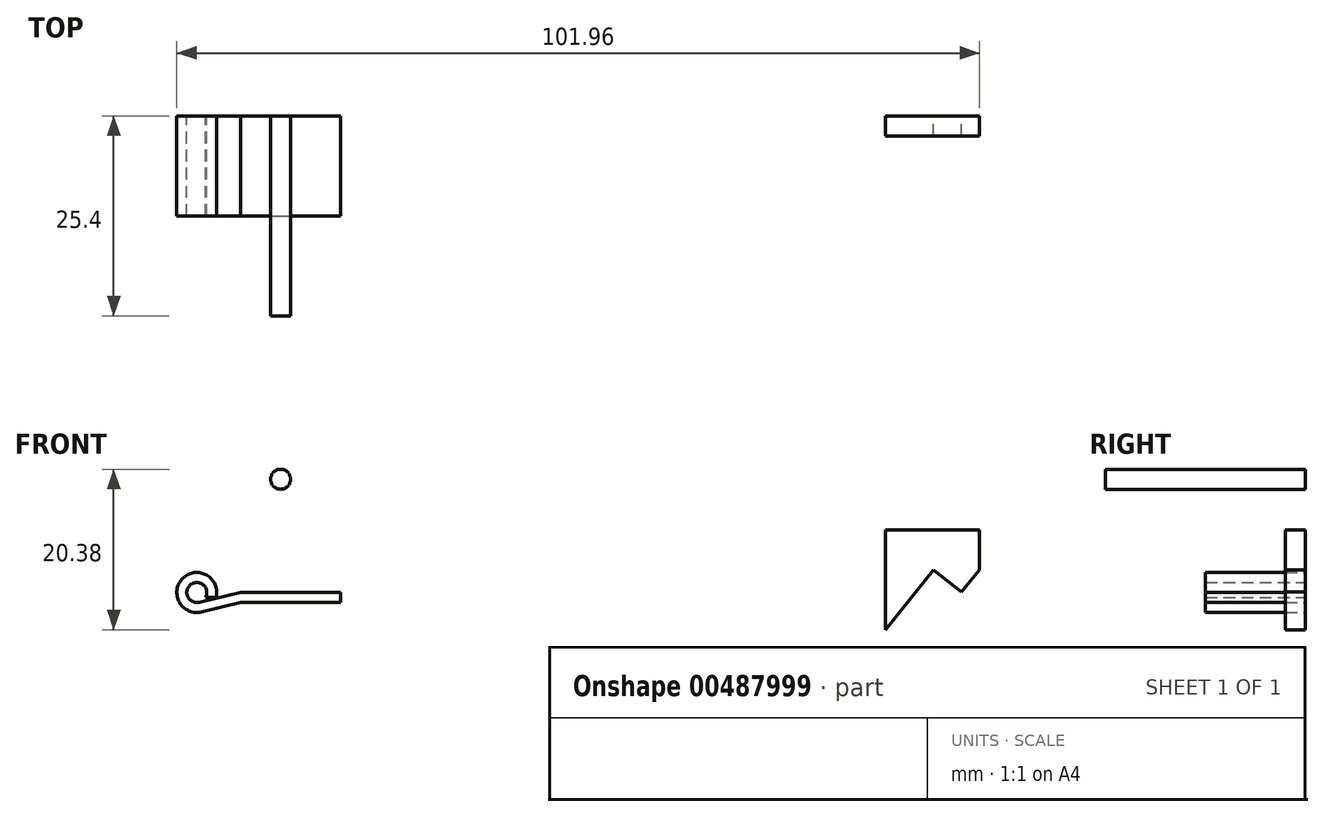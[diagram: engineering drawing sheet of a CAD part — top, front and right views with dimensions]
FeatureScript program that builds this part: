
annotation { "Feature Type Name" : "Feature", "Feature Type Description" : "" }
export const myFeature = defineFeature(function(context is Context, id is Id, definition is map)
    precondition{}
    {
        {
            var Q0;
            Q0=qCreatedBy(makeId("Front.planeOp"),FACE);
            var sketch = newSketch(context, id + "F0", { "sketchPlane" : qUnion([Q0])});
            skLineSegment(sketch, "E0.bottom", {"start": v(-45.7, 38.1) * mm, "end": v(-20.3, 38.1) * mm});
            skLineSegment(sketch, "E0.top", {"start": v(-45.7, 0) * mm, "end": v(-20.3, 0) * mm});
            skLineSegment(sketch, "E0.left", {"start": v(-45.7, 38.1) * mm, "end": v(-45.7, 0) * mm});
            skLineSegment(sketch, "E0.right", {"start": v(-20.3, 38.1) * mm, "end": v(-20.3, 0) * mm});
            skCircle(sketch, "E1", {"center": v(-38.42, -37.85) * mm, "radius": 1.27 * mm});
            skArc(sketch, "E2", {"start": v(-35.96, -38.46) * mm, "mid": v(-40.21, -36.05) * mm, "end": v(-37.82, -40.31) * mm});
            skLineSegment(sketch, "E3", {"start": v(-32.89, -37.85) * mm, "end": v(-20.19, -37.85) * mm});
            skLineSegment(sketch, "E4", {"start": v(-32.89, -39.12) * mm, "end": v(-20.19, -39.12) * mm});
            skLineSegment(sketch, "E5", {"start": v(-20.19, -39.12) * mm, "end": v(-32.89, -39.12) * mm});
            skLineSegment(sketch, "E6", {"start": v(-32.89, -39.12) * mm, "end": v(-37.82, -40.31) * mm});
            skLineSegment(sketch, "E7", {"start": v(-32.89, -37.85) * mm, "end": v(-38.13, -39.08) * mm});
            skLineSegment(sketch, "E8", {"start": v(-35.96, -38.46) * mm, "end": v(-37.3, -38.46) * mm});
            skLineSegment(sketch, "E9", {"start": v(-20.19, -37.85) * mm, "end": v(-20.19, -39.12) * mm});
            skSolve(sketch);
        }
        {
            var Q0;
            Q0=makeQuery(id+"F0.imprint","IMPRINT",FACE,{"disambiguationData":[TD([[makeQuery(id+"F0.imprint","IMPRINT",EDGE,{"derivedFrom":sQuery(id+"F0.wireOp",EDGE,"E2")}),1.0]])]});
            extrude(context, id + "F1", {"entities" : qUnion([Q0]), "depth" : 12.7 * mm, "offsetDistance" : 25.4 * mm});
        }
        {
            var Q0;
            Q0=qCreatedBy(makeId("Front.planeOp"),FACE);
            var sketch = newSketch(context, id + "F2", { "sketchPlane" : qUnion([Q0])});
            skLineSegment(sketch, "E10", {"start": v(61, -29.87) * mm, "end": v(61, -34.95) * mm});
            skLineSegment(sketch, "E11", {"start": v(61, -34.95) * mm, "end": v(58.71, -37.8) * mm});
            skLineSegment(sketch, "E12", {"start": v(58.71, -37.8) * mm, "end": v(55.18, -34.95) * mm});
            skLineSegment(sketch, "E13", {"start": v(55.18, -34.95) * mm, "end": v(49.05, -42.57) * mm});
            skLineSegment(sketch, "E14", {"start": v(49.05, -42.57) * mm, "end": v(49.05, -29.87) * mm});
            skLineSegment(sketch, "E15", {"start": v(49.05, -29.87) * mm, "end": v(61, -29.87) * mm});
            skSolve(sketch);
        }
        {
            var Q0;
            Q0 = qSketchRegion(id + "F2", true);
            extrude(context, id + "F3", {"entities" : qUnion([Q0]), "depth" : 2.54 * mm, "offsetDistance" : 25.4 * mm});
        }
        {
            var Q0;
            Q0=qCreatedBy(makeId("Front.planeOp"),FACE);
            var sketch = newSketch(context, id + "F4", { "sketchPlane" : qUnion([Q0])});
            skCircle(sketch, "E16", {"center": v(-27.77, -23.46) * mm, "radius": 1.27 * mm});
            skSolve(sketch);
        }
        {
            var Q0;
            Q0 = qSketchRegion(id + "F4", true);
            extrude(context, id + "F5", {"entities" : qUnion([Q0]), "depth" : 25.4 * mm, "offsetDistance" : 25.4 * mm});
        }
    });
